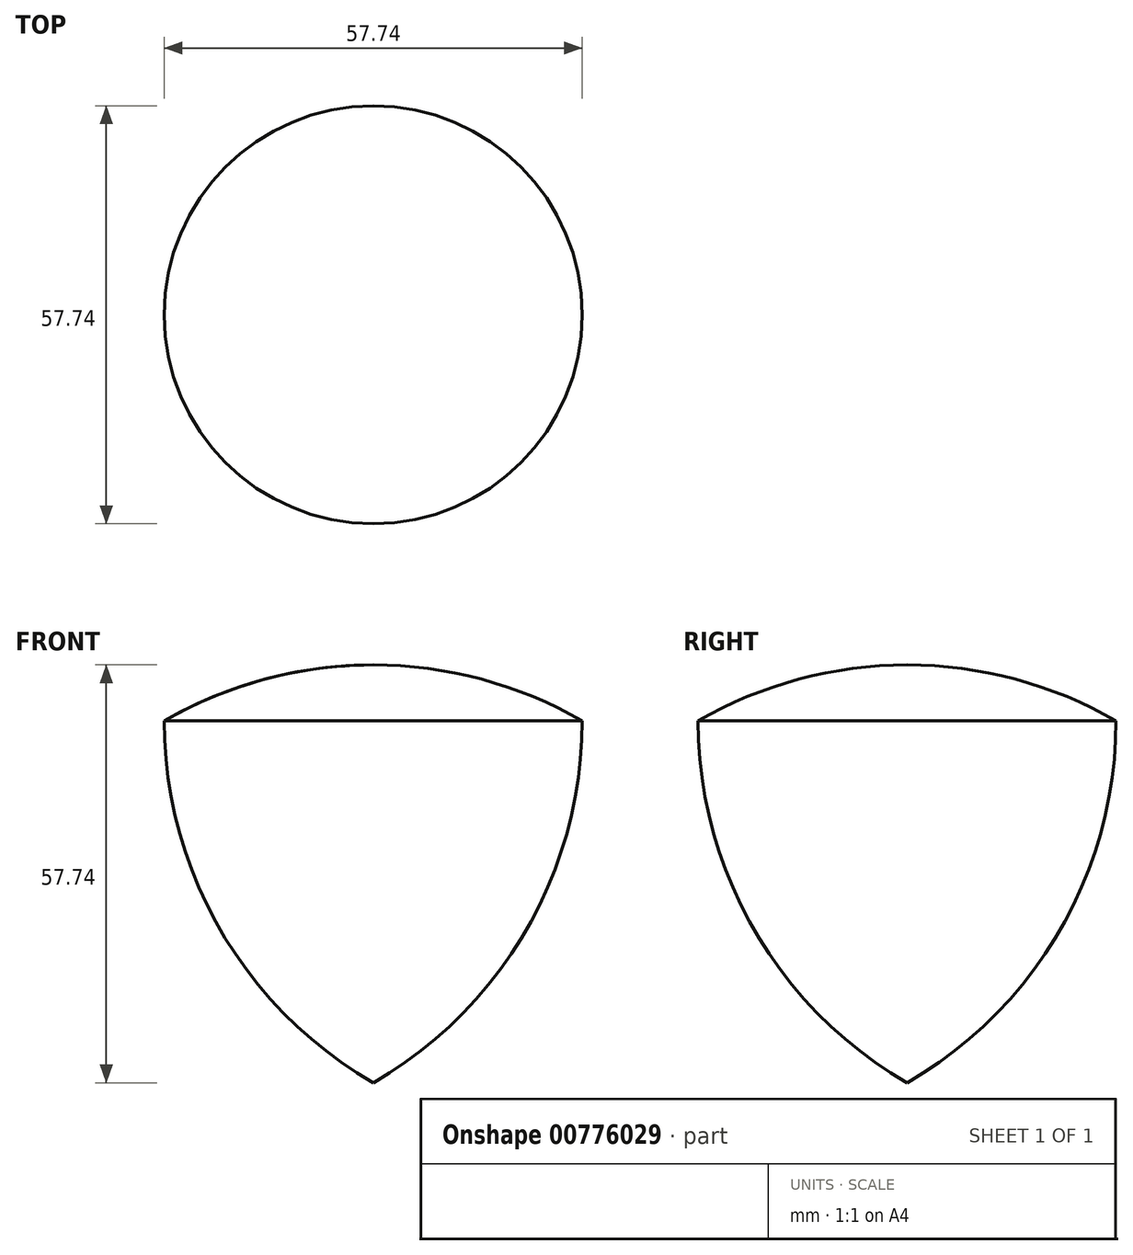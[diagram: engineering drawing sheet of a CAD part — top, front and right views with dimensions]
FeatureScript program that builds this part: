
annotation { "Feature Type Name" : "Feature", "Feature Type Description" : "" }
export const myFeature = defineFeature(function(context is Context, id is Id, definition is map)
    precondition{}
    {
        {
            var Q0;
            Q0=qCreatedBy(makeId("Front.planeOp"),FACE);
            var sketch = newSketch(context, id + "F0", { "sketchPlane" : qUnion([Q0])});
            skLineSegment(sketch, "E0", {"start": v(0, 0) * mm, "end": v(-28.87, 0) * mm, "construction": true});
            skLineSegment(sketch, "E1", {"start": v(-28.87, 0) * mm, "end": v(0, -50) * mm, "construction": true});
            skArc(sketch, "E2", {"start": v(-28.87, 0) * mm, "mid": v(-21.13, -28.87) * mm, "end": v(0, -50) * mm});
            skArc(sketch, "E3", {"start": v(0, 7.74) * mm, "mid": v(-14.94, 5.77) * mm, "end": v(-28.87, 0) * mm});
            skLineSegment(sketch, "E4", {"start": v(0, 7.74) * mm, "end": v(0, -50) * mm, "construction": true});
            skSolve(sketch);
        }
        {
            var Q0;
            Q0=sQuery(id+"F0.wireOp",EDGE,"E2");
            var Q1;
            Q1=sQuery(id+"F0.wireOp",EDGE,"E3");
            var Q2;
            Q2=sQuery(id+"F0.wireOp",EDGE,"E4");
            revolve(context, id + "F1", {"bodyType" : ToolBodyType.SURFACE, "surfaceOperationType" : NewSurfaceOperationType.NEW, "surfaceEntities" : qUnion([Q0, Q1]), "axis" : qUnion([Q2]), "revolveType" : RevolveType.FULL});
        }
    });
